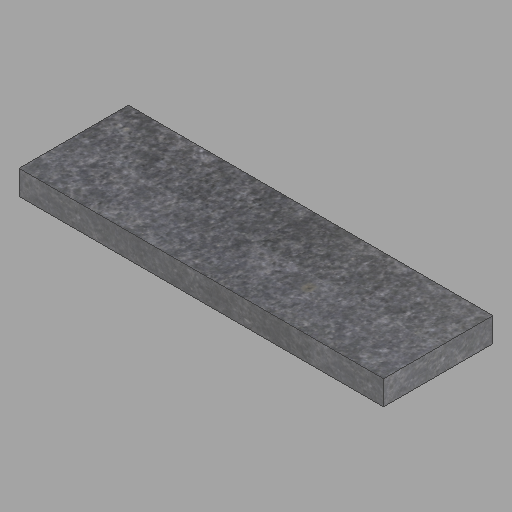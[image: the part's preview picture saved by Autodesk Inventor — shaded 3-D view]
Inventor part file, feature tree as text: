
AUTODESK INVENTOR PART (.ipt)
format: ipt  version: 2022.2 (Build 262287010, 287A)  size: 209,920 bytes
history: native  units: in
note: dims shown in document units (in); Inventor stores cm internally (conversion verified against a paired STEP export)
features: extrude x1, sketch x1
ambient origin geometry x8: Origin, YZ Plane, XZ Plane, XY Plane, X Axis, Y Axis, Z Axis, Center Point
bodies: Solid1 (feature_tree)
feature tree (2):
  extrude  "Extrusion1"  Depth=18.0in
  sketch  "Sketch1"  dims[d0=60.0in d1=18.0in d2=4.0in d3=0.0in]
